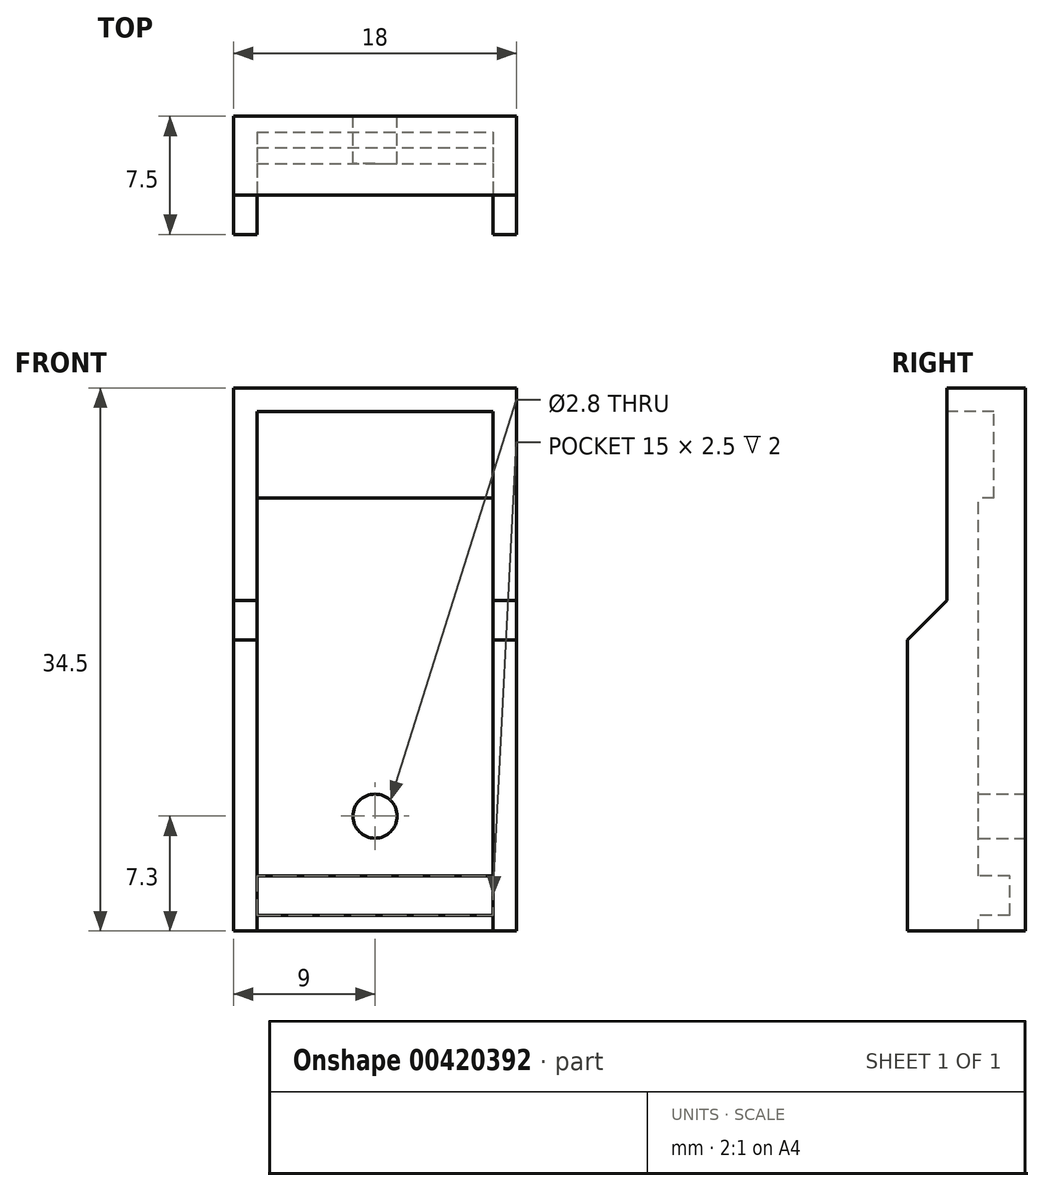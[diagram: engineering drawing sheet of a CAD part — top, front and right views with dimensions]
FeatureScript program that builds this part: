
annotation { "Feature Type Name" : "Feature", "Feature Type Description" : "" }
export const myFeature = defineFeature(function(context is Context, id is Id, definition is map)
    precondition{}
    {
        {
            var Q0;
            Q0=qCreatedBy(makeId("Front.planeOp"),FACE);
            var sketch = newSketch(context, id + "F0", { "sketchPlane" : qUnion([Q0])});
            skLineSegment(sketch, "E0.bottom", {"start": v(0, 0) * mm, "end": v(15, 0) * mm});
            skLineSegment(sketch, "E0.top", {"start": v(0, 33) * mm, "end": v(15, 33) * mm});
            skLineSegment(sketch, "E0.left", {"start": v(0, 0) * mm, "end": v(0, 33) * mm});
            skLineSegment(sketch, "E0.right", {"start": v(15, 0) * mm, "end": v(15, 33) * mm});
            skSolve(sketch);
        }
        {
            var Q0;
            Q0=qSketchRegion(id+"F0",true);
            extrude(context, id + "F1", {"entities" : qUnion([Q0]), "depth" : 3 * mm});
        }
        {
            var Q0;
            Q0=makeQuery(id+"F1.opExtrude","CAP_FACE",FACE,{"disambiguationData":[OSD([sQuery(id+"F0.wireOp",EDGE,"E0.bottom"),sQuery(id+"F0.wireOp",EDGE,"E0.top"),sQuery(id+"F0.wireOp",EDGE,"E0.left"),sQuery(id+"F0.wireOp",EDGE,"E0.right")])],"isStart":false});
            var sketch = newSketch(context, id + "F2", { "sketchPlane" : qUnion([Q0])});
            skLineSegment(sketch, "E1", {"start": v(0, 0) * mm, "end": v(0, 1) * mm});
            skLineSegment(sketch, "E2.bottom", {"start": v(0, 1) * mm, "end": v(15, 1) * mm});
            skLineSegment(sketch, "E2.top", {"start": v(0, 3.5) * mm, "end": v(15, 3.5) * mm});
            skLineSegment(sketch, "E2.left", {"start": v(0, 1) * mm, "end": v(0, 3.5) * mm});
            skLineSegment(sketch, "E2.right", {"start": v(15, 1) * mm, "end": v(15, 3.5) * mm});
            skSolve(sketch);
        }
        {
            var Q0;
            Q0=qSketchRegion(id+"F2",true);
            extrude(context, id + "F3", {"entities" : qUnion([Q0]), "operationType" : NewBodyOperationType.REMOVE, "oppositeDirection" : true, "depth" : 2 * mm});
        }
        {
            var Q0;
            {var subQ0=sQuery(id+"F0.wireOp",EDGE,"E0.top");var subQ1=sQuery(id+"F0.wireOp",EDGE,"E0.left");var subQ2=sQuery(id+"F0.wireOp",EDGE,"E0.right");Q0=makeQuery(id+"F3.boolean.opBoolean","SPLIT",FACE,{"disambiguationData":[TD([makeQuery(id+"F1.opExtrude","SWEPT_FACE",FACE,{"disambiguationData":[OSD([subQ0])]})])],"derivedFrom":makeQuery(id+"F1.opExtrude","CAP_FACE",FACE,{"disambiguationData":[OSD([sQuery(id+"F0.wireOp",EDGE,"E0.bottom"),subQ0,subQ1,subQ2])],"isStart":false})});}
            var sketch = newSketch(context, id + "F4", { "sketchPlane" : qUnion([Q0])});
            skLineSegment(sketch, "E3.bottom", {"start": v(0, 33) * mm, "end": v(15, 33) * mm});
            skLineSegment(sketch, "E3.top", {"start": v(0, 27.5) * mm, "end": v(15, 27.5) * mm});
            skLineSegment(sketch, "E3.left", {"start": v(0, 33) * mm, "end": v(0, 27.5) * mm});
            skLineSegment(sketch, "E3.right", {"start": v(15, 33) * mm, "end": v(15, 27.5) * mm});
            skSolve(sketch);
        }
        {
            var Q0;
            Q0=qSketchRegion(id+"F4",true);
            extrude(context, id + "F5", {"entities" : qUnion([Q0]), "operationType" : NewBodyOperationType.REMOVE, "oppositeDirection" : true, "depth" : 1 * mm});
        }
        {
            var Q0;
            Q0=makeQuery(id+"F1.opExtrude","CAP_FACE",FACE,{"disambiguationData":[OSD([sQuery(id+"F0.wireOp",EDGE,"E0.bottom"),sQuery(id+"F0.wireOp",EDGE,"E0.top"),sQuery(id+"F0.wireOp",EDGE,"E0.left"),sQuery(id+"F0.wireOp",EDGE,"E0.right")])],"isStart":true});
            var sketch = newSketch(context, id + "F6", { "sketchPlane" : qUnion([Q0])});
            skLineSegment(sketch, "E4", {"start": v(-7.5, 0) * mm, "end": v(-7.5, 7.3) * mm});
            skCircle(sketch, "E5", {"center": v(-7.5, 7.3) * mm, "radius": 1.4 * mm});
            skSolve(sketch);
        }
        {
            var Q0;
            Q0=qSketchRegion(id+"F6",true);
            extrude(context, id + "F7", {"entities" : qUnion([Q0]), "operationType" : NewBodyOperationType.REMOVE, "oppositeDirection" : true, "depth" : 25 * mm});
        }
        {
            var Q0;
            Q0=makeQuery(id+"F1.opExtrude","SWEPT_FACE",FACE,{"disambiguationData":[OSD([sQuery(id+"F0.wireOp",EDGE,"E0.top")])]});
            var sketch = newSketch(context, id + "F8", { "sketchPlane" : qUnion([Q0])});
            skLineSegment(sketch, "E6", {"start": v(0, 0) * mm, "end": v(-1.5, 0) * mm});
            skLineSegment(sketch, "E7", {"start": v(-1.5, 0) * mm, "end": v(-1.5, -5) * mm});
            skLineSegment(sketch, "E8", {"start": v(-1.5, -5) * mm, "end": v(15, -5) * mm});
            skLineSegment(sketch, "E9", {"start": v(15, -5) * mm, "end": v(16.5, -5) * mm});
            skLineSegment(sketch, "E10", {"start": v(16.5, -5) * mm, "end": v(16.5, 0) * mm});
            skLineSegment(sketch, "E11", {"start": v(16.5, 0) * mm, "end": v(0, 0) * mm});
            skSolve(sketch);
        }
        {
            var Q0;
            Q0=qSketchRegion(id+"F8",true);
            extrude(context, id + "F9", {"entities" : qUnion([Q0]), "operationType" : NewBodyOperationType.ADD, "depth" : 1.5 * mm});
        }
        {
            var Q0;
            Q0=makeQuery(id+"F9.opExtrude","SWEPT_FACE",FACE,{"disambiguationData":[OSD([sQuery(id+"F8.wireOp",EDGE,"E10")])]});
            var sketch = newSketch(context, id + "F10", { "sketchPlane" : qUnion([Q0])});
            skLineSegment(sketch, "E12", {"start": v(-5, 34.5) * mm, "end": v(-5, 0) * mm});
            skLineSegment(sketch, "E13", {"start": v(0, 0) * mm, "end": v(-5, 0) * mm});
            skLineSegment(sketch, "E14", {"start": v(0, 34.5) * mm, "end": v(0, 0) * mm});
            skLineSegment(sketch, "E15", {"start": v(-5, 34.5) * mm, "end": v(0, 34.5) * mm});
            skLineSegment(sketch, "E16", {"start": v(-5, 0) * mm, "end": v(-7.5, 0) * mm});
            skLineSegment(sketch, "E17", {"start": v(-7.5, 0) * mm, "end": v(-7.5, 21) * mm});
            skLineSegment(sketch, "E18", {"start": v(-7.5, 21) * mm, "end": v(-5, 21) * mm});
            skSolve(sketch);
        }
        {
            var Q0;
            Q0=qSketchRegion(id+"F10",true);
            var Q1;
            Q1=makeQuery(id+"F1.opExtrude","SWEPT_FACE",FACE,{"disambiguationData":[OSD([sQuery(id+"F0.wireOp",EDGE,"E0.right")])]});
            extrude(context, id + "F11", {"entities" : qUnion([Q0]), "operationType" : NewBodyOperationType.ADD, "endBound" : BoundingType.UP_TO_SURFACE, "oppositeDirection" : true, "endBoundEntityFace" : qUnion([Q1]), "depth" : 25 * mm});
        }
        {
            var Q0;
            Q0=qCreatedBy(makeId("Right.planeOp"),FACE);
            cPlane(context, id + "F12", {"entities" : qUnion([Q0]), "cplaneType" : CPlaneType.OFFSET, "offset" : 7.5 * mm, "width" : 150 * mm, "height" : 150 * mm});
        }
        {
            var Q0;
            Q0=makeQuery(id+"F1.opExtrude","SWEPT_BODY",BODY,{"disambiguationData":[OSD([sQuery(id+"F0.wireOp",EDGE,"E0.bottom"),sQuery(id+"F0.wireOp",EDGE,"E0.top"),sQuery(id+"F0.wireOp",EDGE,"E0.left"),sQuery(id+"F0.wireOp",EDGE,"E0.right")])]});
            var Q1;
            Q1=qCreatedBy(id+"F12.planeOp",FACE);
            mirror(context, id + "F13", {"operationType" : NewBodyOperationType.ADD, "entities" : qUnion([Q0]), "mirrorPlane" : qUnion([Q1])});
        }
        {
            var Q0;
            Q0=makeQuery(id+"F11.opExtrude","SWEPT_EDGE",EDGE,{"disambiguationData":[OSD([sQuery(id+"F10.wireOp",EDGE,"E17"),sQuery(id+"F10.wireOp",EDGE,"E18")])]});
            var Q1;
            Q1=makeQuery(id+"F13.opPattern","COPY",EDGE,{"derivedFrom":makeQuery(id+"F11.opExtrude","SWEPT_EDGE",EDGE,{"disambiguationData":[OSD([sQuery(id+"F10.wireOp",EDGE,"E17"),sQuery(id+"F10.wireOp",EDGE,"E18")])]}),"instanceName":"1"});
            chamfer(context, id + "F14", {"entities" : qUnion([Q0, Q1]), "width" : 2.5 * mm, "tangentPropagation" : true});
        }
        {
            var Q0;
            Q0=makeQuery(id+"F11.boolean.opBoolean","MERGE",FACE,{"derivedFrom":[makeQuery(id+"F9.opExtrude","SWEPT_FACE",FACE,{"disambiguationData":[OSD([sQuery(id+"F8.wireOp",EDGE,"E10")])]}),makeQuery(id+"F11.opExtrude","CAP_FACE",FACE,{"disambiguationData":[OSD([sQuery(id+"F10.wireOp",EDGE,"E12"),sQuery(id+"F10.wireOp",EDGE,"E13"),sQuery(id+"F10.wireOp",EDGE,"E14"),sQuery(id+"F10.wireOp",EDGE,"E15"),sQuery(id+"F10.wireOp",EDGE,"E16"),sQuery(id+"F10.wireOp",EDGE,"E17"),sQuery(id+"F10.wireOp",EDGE,"E18")])],"isStart":true})]});
            var sketch = newSketch(context, id + "F15", { "sketchPlane" : qUnion([Q0])});
            skLineSegment(sketch, "E19", {"start": v(0, 0) * mm, "end": v(-3, 0) * mm});
            skLineSegment(sketch, "E20", {"start": v(-3, 0) * mm, "end": v(-3, 34.5) * mm});
            skLineSegment(sketch, "E21", {"start": v(-3, 34.5) * mm, "end": v(0, 34.5) * mm});
            skLineSegment(sketch, "E22", {"start": v(0, 34.5) * mm, "end": v(0, 0) * mm});
            skSolve(sketch);
        }
        {
            var Q0;
            Q0=qSketchRegion(id+"F15",true);
            extrude(context, id + "F16", {"entities" : qUnion([Q0]), "operationType" : NewBodyOperationType.ADD, "depth" : 8.25 * mm, "offsetDistance" : 25 * mm});
        }
        {
            var Q0;
            Q0=makeQuery(id+"F16.opExtrude","SWEPT_FACE",FACE,{"disambiguationData":[OSD([sQuery(id+"F15.wireOp",EDGE,"E20")])]});
            var sketch = newSketch(context, id + "F17", { "sketchPlane" : qUnion([Q0])});
            skLineSegment(sketch, "E23.bottom", {"start": v(24.75, 34.5) * mm, "end": v(16.5, 34.5) * mm});
            skLineSegment(sketch, "E23.top", {"start": v(24.75, 24.5) * mm, "end": v(16.5, 24.5) * mm});
            skLineSegment(sketch, "E23.left", {"start": v(24.75, 34.5) * mm, "end": v(24.75, 24.5) * mm});
            skLineSegment(sketch, "E23.right", {"start": v(16.5, 34.5) * mm, "end": v(16.5, 24.5) * mm});
            skSolve(sketch);
        }
        {
            var Q0;
            Q0=qSketchRegion(id+"F17",true);
            extrude(context, id + "F18", {"entities" : qUnion([Q0]), "operationType" : NewBodyOperationType.REMOVE, "oppositeDirection" : true, "depth" : 25 * mm, "offsetDistance" : 25 * mm});
        }
        {
            var Q0;
            Q0=makeQuery(id+"F16.opExtrude","SWEPT_FACE",FACE,{"disambiguationData":[OSD([sQuery(id+"F15.wireOp",EDGE,"E20")])]});
            extrude(context, id + "F19", {"entities" : qUnion([Q0]), "operationType" : NewBodyOperationType.ADD, "depth" : 6 * mm, "offsetDistance" : 25 * mm});
        }
        {
            var Q0;
            {var subQ0=makeQuery(id+"F11.boolean.opBoolean","MERGE",FACE,{"derivedFrom":[makeQuery(id+"F9.boolean.opBoolean","MERGE",FACE,{"derivedFrom":[makeQuery(id+"F1.opExtrude","CAP_FACE",FACE,{"disambiguationData":[OSD([sQuery(id+"F0.wireOp",EDGE,"E0.bottom"),sQuery(id+"F0.wireOp",EDGE,"E0.top"),sQuery(id+"F0.wireOp",EDGE,"E0.left"),sQuery(id+"F0.wireOp",EDGE,"E0.right")])],"isStart":true}),makeQuery(id+"F9.opExtrude","SWEPT_FACE",FACE,{"disambiguationData":[OSD([sQuery(id+"F8.wireOp",EDGE,"E6"),sQuery(id+"F8.wireOp",EDGE,"E11")])]})]}),makeQuery(id+"F11.opExtrude","SWEPT_FACE",FACE,{"disambiguationData":[OSD([sQuery(id+"F10.wireOp",EDGE,"E14")])]})]});Q0=makeQuery(id+"F16.boolean.opBoolean","MERGE",FACE,{"derivedFrom":[makeQuery(id+"F13.boolean.opBoolean","MERGE",FACE,{"derivedFrom":[subQ0,makeQuery(id+"F13.opPattern","COPY",FACE,{"derivedFrom":subQ0,"instanceName":"1"})]}),makeQuery(id+"F16.opExtrude","SWEPT_FACE",FACE,{"disambiguationData":[OSD([sQuery(id+"F15.wireOp",EDGE,"E22")])]})]});}
            var sketch = newSketch(context, id + "F20", { "sketchPlane" : qUnion([Q0])});
            skLineSegment(sketch, "E24", {"start": v(-7.5, 7.3) * mm, "end": v(-7.5, 8.3) * mm});
            skLineSegment(sketch, "E25", {"start": v(-7.5, 8.3) * mm, "end": v(-24.75, 8.3) * mm});
            skLineSegment(sketch, "E26", {"start": v(-24.75, 8.3) * mm, "end": v(-20.75, 8.3) * mm});
            skLineSegment(sketch, "E27", {"start": v(-20.75, 8.3) * mm, "end": v(-20.75, 18.3) * mm});
            skCircle(sketch, "E28", {"center": v(-20.75, 8.3) * mm, "radius": 1.4 * mm});
            skCircle(sketch, "E29", {"center": v(-20.75, 18.3) * mm, "radius": 1.4 * mm});
            skSolve(sketch);
        }
        {
            var Q0;
            Q0=qSketchRegion(id+"F20",true);
            extrude(context, id + "F21", {"entities" : qUnion([Q0]), "operationType" : NewBodyOperationType.REMOVE, "oppositeDirection" : true, "depth" : 25 * mm, "offsetDistance" : 25 * mm});
        }
        {
            var Q0;
            {var subQ0=sQuery(id+"F17.wireOp",EDGE,"E23.top");Q0=makeQuery(id+"F19.boolean.opBoolean","MERGE",FACE,{"derivedFrom":[makeQuery(id+"F18.boolean.opBoolean","COPY",FACE,{"derivedFrom":makeQuery(id+"F18.opExtrude","SWEPT_FACE",FACE,{"disambiguationData":[OSD([subQ0])]})}),makeQuery(id+"F19.opExtrude","SWEPT_FACE",FACE,{"disambiguationData":[OSD([subQ0])]})]});}
            extrude(context, id + "F22", {"entities" : qUnion([Q0]), "operationType" : NewBodyOperationType.REMOVE, "oppositeDirection" : true, "depth" : 25 * mm, "offsetDistance" : 25 * mm});
        }
    });
